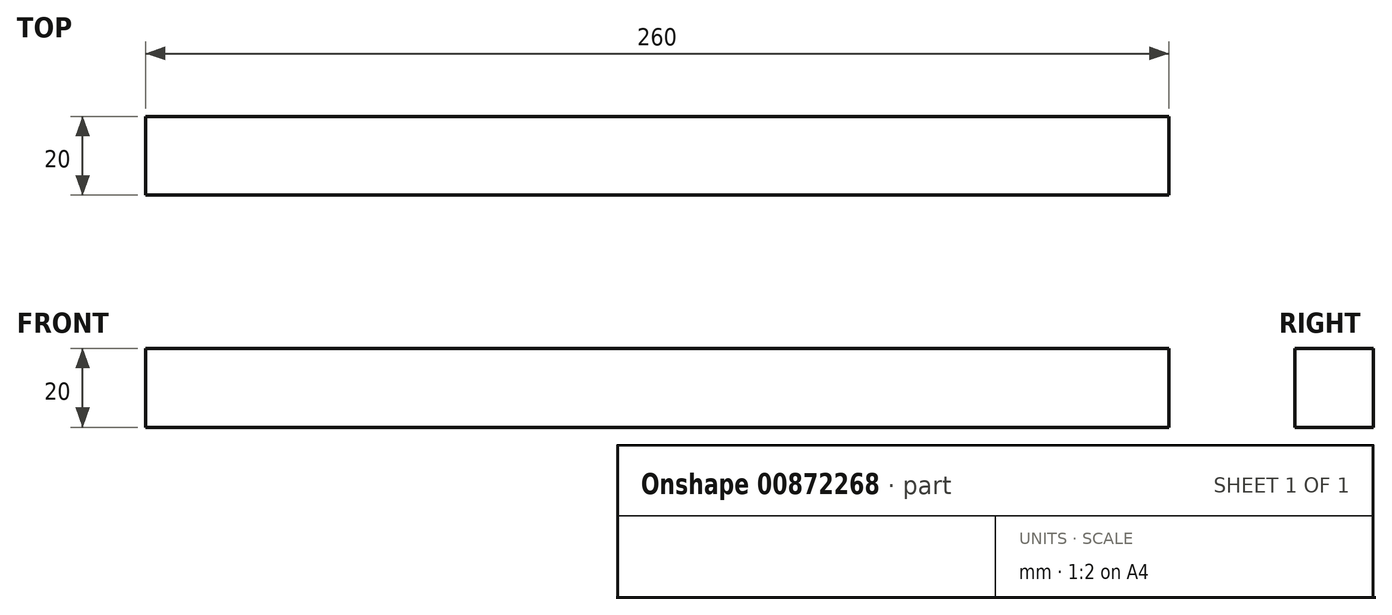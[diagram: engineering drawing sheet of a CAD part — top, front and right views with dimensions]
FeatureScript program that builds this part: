
annotation { "Feature Type Name" : "Feature", "Feature Type Description" : "" }
export const myFeature = defineFeature(function(context is Context, id is Id, definition is map)
    precondition{}
    {
        {
            var Q0;
            Q0=qCreatedBy(makeId("Front.planeOp"),FACE);
            var sketch = newSketch(context, id + "F0", { "sketchPlane" : qUnion([Q0])});
            skLineSegment(sketch, "E0.bottom", {"start": v(130, -10) * mm, "end": v(-130, -10) * mm});
            skLineSegment(sketch, "E0.top", {"start": v(130, 10) * mm, "end": v(-130, 10) * mm});
            skLineSegment(sketch, "E0.left", {"start": v(130, -10) * mm, "end": v(130, 10) * mm});
            skLineSegment(sketch, "E0.right", {"start": v(-130, -10) * mm, "end": v(-130, 10) * mm});
            skPoint(sketch, "E0.middle", {"position": v(0, 0) * mm});
            skSolve(sketch);
        }
        {
            var Q0;
            Q0=makeQuery(id+"F0.imprint","IMPRINT",FACE,{"disambiguationData":[TD([[makeQuery(id+"F0.imprint","IMPRINT",EDGE,{"derivedFrom":sQuery(id+"F0.wireOp",EDGE,"E0.bottom")}),-1.0]])]});
            extrude(context, id + "F1", {"entities" : qUnion([Q0]), "endBound" : BoundingType.SYMMETRIC, "depth" : 20 * mm, "offsetDistance" : 25 * mm});
        }
    });
